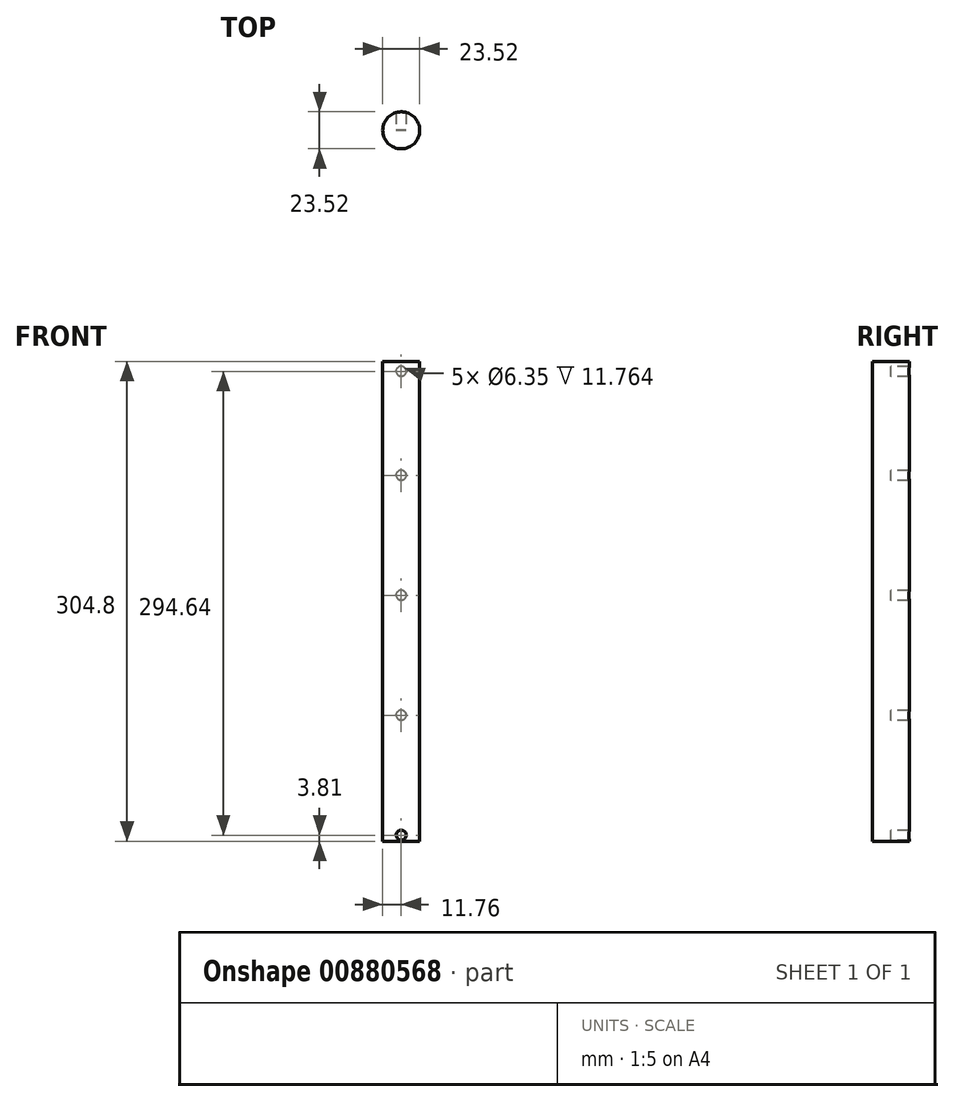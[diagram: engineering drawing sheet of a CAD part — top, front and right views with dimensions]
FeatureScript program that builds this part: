
annotation { "Feature Type Name" : "Feature", "Feature Type Description" : "" }
export const myFeature = defineFeature(function(context is Context, id is Id, definition is map)
    precondition{}
    {
        {
            var Q0;
            Q0=qCreatedBy(makeId("Top.planeOp"),FACE);
            var sketch = newSketch(context, id + "F0", { "sketchPlane" : qUnion([Q0])});
            skCircle(sketch, "E0", {"center": v(0, 0) * mm, "radius": 11.76 * mm});
            skSolve(sketch);
        }
        {
            var Q0;
            Q0 = qSketchRegion(id + "F0", true);
            extrude(context, id + "F1", {"entities" : qUnion([Q0]), "depth" : 304.8 * mm, "offsetDistance" : 25.4 * mm});
        }
        {
            var Q0;
            Q0=qCreatedBy(makeId("Front.planeOp"),FACE);
            var sketch = newSketch(context, id + "F2", { "sketchPlane" : qUnion([Q0])});
            skCircle(sketch, "E1", {"center": v(0, 298.45) * mm, "radius": 2.38 * mm});
            skCircle(sketch, "E2", {"center": v(0, 232.4) * mm, "radius": 2.38 * mm});
            skCircle(sketch, "E3", {"center": v(0, 156.21) * mm, "radius": 2.38 * mm});
            skCircle(sketch, "E4", {"center": v(0, 80) * mm, "radius": 2.38 * mm});
            skCircle(sketch, "E5", {"center": v(0, 3.81) * mm, "radius": 2.38 * mm});
            skSolve(sketch);
        }
        {
            var Q0;
            Q0=sQuery(id+"F2.wireOp",VERTEX,"E3.center");
            var Q1;
            Q1=sQuery(id+"F2.wireOp",VERTEX,"E4.center");
            var Q2;
            Q2=sQuery(id+"F2.wireOp",VERTEX,"E5.center");
            var Q3;
            Q3=sQuery(id+"F2.wireOp",VERTEX,"E2.center");
            var Q4;
            Q4=sQuery(id+"F2.wireOp",VERTEX,"E1.center");
            var Q5;
            Q5=makeQuery(id+"F1.opExtrude","SWEPT_BODY",BODY,{"disambiguationData":[OSD([sQuery(id+"F0.wireOp",EDGE,"E0")])]});
            hole(context, id + "F3", {"style" : HoleStyle.SIMPLE, "endStyle" : HoleEndStyle.THROUGH, "holeDiameter" : 6.35 * mm, "majorDiameter" : 6.35 * mm, "isTappedThrough" : true, "tappedDepth" : 12.7 * mm, "tapClearance" : 3, "locations" : qUnion([Q0, Q1, Q2, Q3, Q4]), "scope" : qUnion([Q5])});
        }
    });
